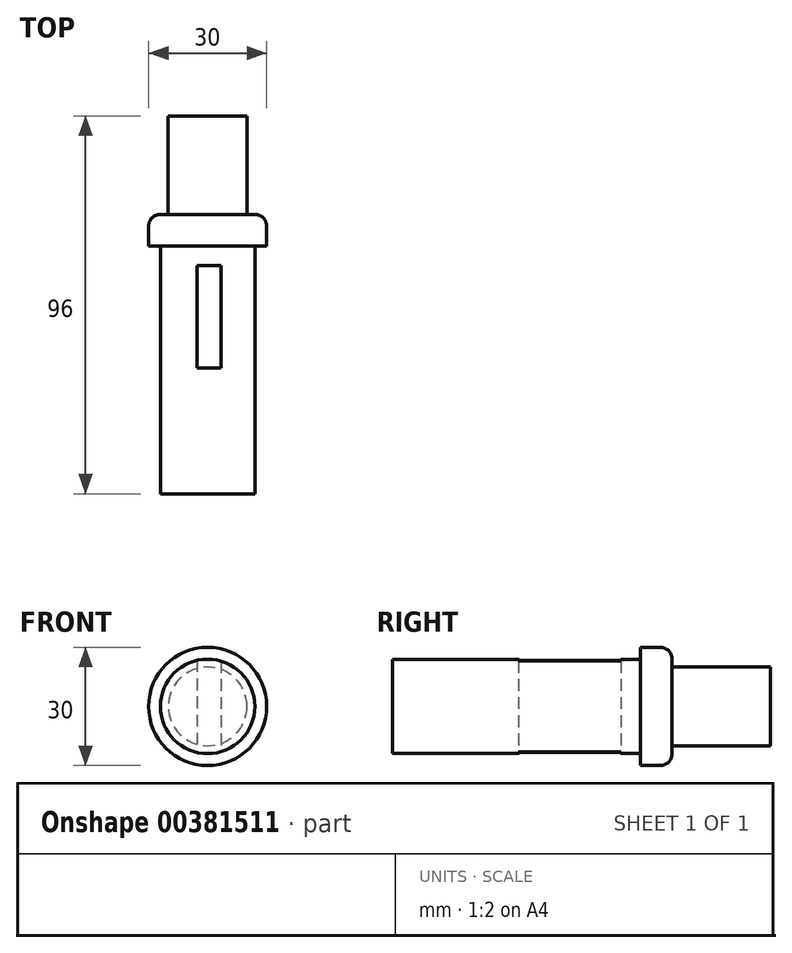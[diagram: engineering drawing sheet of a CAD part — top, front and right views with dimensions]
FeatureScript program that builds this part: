
annotation { "Feature Type Name" : "Feature", "Feature Type Description" : "" }
export const myFeature = defineFeature(function(context is Context, id is Id, definition is map)
    precondition{}
    {
        {
            var Q0;
            Q0=qCreatedBy(makeId("Front.planeOp"),FACE);
            var sketch = newSketch(context, id + "F0", { "sketchPlane" : qUnion([Q0])});
            skCircle(sketch, "E0", {"center": v(18.57, 16.28) * mm, "radius": 12 * mm});
            skSolve(sketch);
        }
        {
            var Q0;
            Q0=makeQuery(id+"F0.imprint","IMPRINT",FACE,{"disambiguationData":[TD([[makeQuery(id+"F0.imprint","IMPRINT",EDGE,{"derivedFrom":sQuery(id+"F0.wireOp",EDGE,"E0")}),1.0]])]});
            extrude(context, id + "F1", {"entities" : qUnion([Q0]), "depth" : 63 * mm});
        }
        {
            var Q0;
            Q0=makeQuery(id+"F1.opExtrude","CAP_FACE",FACE,{"disambiguationData":[OSD([sQuery(id+"F0.wireOp",EDGE,"E0")])],"isStart":true});
            var sketch = newSketch(context, id + "F2", { "sketchPlane" : qUnion([Q0])});
            skCircle(sketch, "E1", {"center": v(-18.57, 16.28) * mm, "radius": 15 * mm});
            skSolve(sketch);
        }
        {
            var Q0;
            Q0=makeQuery(id+"F2.imprint","IMPRINT",FACE,{"disambiguationData":[TD([[makeQuery(id+"F2.imprint","IMPRINT",EDGE,{"derivedFrom":sQuery(id+"F2.wireOp",EDGE,"E1")}),1.0]])]});
            var Q1;
            Q1=makeQuery(id+"F2.imprint","IMPRINT",FACE,{"disambiguationData":[TD([[makeQuery(id+"F2.imprint","IMPRINT",EDGE,{"derivedFrom":makeQuery(id+"F1.opExtrude","CAP_EDGE",EDGE,{"disambiguationData":[OSD([sQuery(id+"F0.wireOp",EDGE,"E0")])],"isStart":true})}),-1.0]])]});
            extrude(context, id + "F3", {"entities" : qUnion([Q0, Q1]), "operationType" : NewBodyOperationType.ADD, "depth" : 8 * mm});
        }
        {
            var Q0;
            Q0=makeQuery(id+"F3.opExtrude","CAP_FACE",FACE,{"disambiguationData":[OSD([sQuery(id+"F2.wireOp",EDGE,"E1")])],"isStart":false});
            var sketch = newSketch(context, id + "F4", { "sketchPlane" : qUnion([Q0])});
            skCircle(sketch, "E2", {"center": v(-18.57, 16.28) * mm, "radius": 10 * mm});
            skSolve(sketch);
        }
        {
            var Q0;
            Q0=makeQuery(id+"F4.imprint","IMPRINT",FACE,{"disambiguationData":[TD([[makeQuery(id+"F4.imprint","IMPRINT",EDGE,{"derivedFrom":sQuery(id+"F4.wireOp",EDGE,"E2")}),1.0]])]});
            extrude(context, id + "F5", {"entities" : qUnion([Q0]), "operationType" : NewBodyOperationType.ADD, "depth" : 25 * mm});
        }
        {
            var Q0;
            Q0=makeQuery(id+"F3.opExtrude","CAP_EDGE",EDGE,{"disambiguationData":[OSD([sQuery(id+"F2.wireOp",EDGE,"E1")])],"isStart":false});
            fillet(context, id + "F6", {"entities" : qUnion([Q0]), "radius" : 3 * mm, "tangentPropagation" : true, "allowEdgeOverflow" : false});
        }
        {
            var Q0;
            Q0=qCreatedBy(makeId("Top.planeOp"),FACE);
            var sketch = newSketch(context, id + "F7", { "sketchPlane" : qUnion([Q0])});
            skLineSegment(sketch, "E3", {"start": v(18.91, 8) * mm, "end": v(18.91, -5) * mm});
            skLineSegment(sketch, "E4", {"start": v(18.91, -5) * mm, "end": v(15.91, -5) * mm});
            skLineSegment(sketch, "E5", {"start": v(15.91, -5) * mm, "end": v(15.91, -31) * mm});
            skLineSegment(sketch, "E6", {"start": v(15.91, -31) * mm, "end": v(18.91, -31) * mm});
            skLineSegment(sketch, "E7.MirrorCS", {"start": v(18.91, -5) * mm, "end": v(21.91, -5) * mm});
            skLineSegment(sketch, "E8.MirrorCS", {"start": v(21.91, -5) * mm, "end": v(21.91, -31) * mm});
            skLineSegment(sketch, "E9.MirrorCS", {"start": v(21.91, -31) * mm, "end": v(18.91, -31) * mm});
            skSolve(sketch);
        }
        {
            var Q0;
            Q0=makeQuery(id+"F7.imprint","IMPRINT",FACE,{"disambiguationData":[TD([[makeQuery(id+"F7.imprint","IMPRINT",EDGE,{"derivedFrom":sQuery(id+"F7.wireOp",EDGE,"E4")}),1.0]])]});
            extrude(context, id + "F8", {"entities" : qUnion([Q0]), "operationType" : NewBodyOperationType.REMOVE, "endBound" : BoundingType.THROUGH_ALL, "depth" : 25 * mm});
        }
    });
